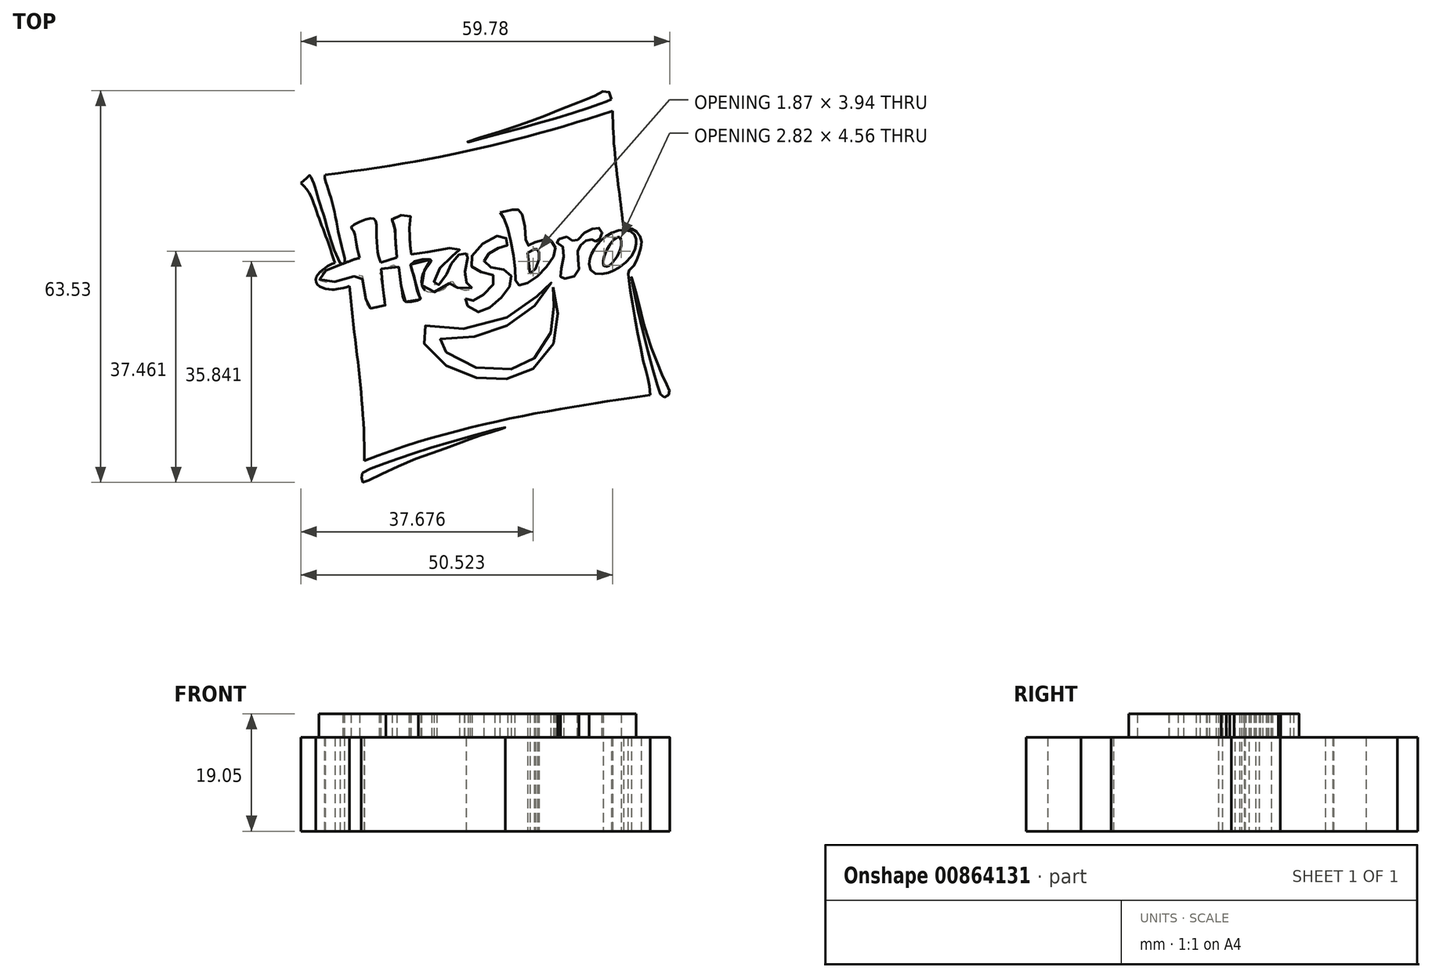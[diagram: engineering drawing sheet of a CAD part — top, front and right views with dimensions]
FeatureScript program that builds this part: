
annotation { "Feature Type Name" : "Feature", "Feature Type Description" : "" }
export const myFeature = defineFeature(function(context is Context, id is Id, definition is map)
    precondition{}
    {
        {
            var Q0;
            Q0=qCreatedBy(makeId("Top.planeOp"),FACE);
            var sketch = newSketch(context, id + "F0", { "sketchPlane" : qUnion([Q0])});
            skFitSpline(sketch, "E0", {"points": [v(-6.58, -8.68) * mm, v(-52.97, -19.35) * mm], "startDerivative": vector(-37.99, -5.76) * mm, "endDerivative": vector(-49.48, -19.31) * mm});
            skFitSpline(sketch, "E1", {"points": [v(-52.97, -19.35) * mm, v(-55.37, 8.98) * mm], "startDerivative": vector(0.45, 28.63) * mm, "endDerivative": vector(-2.64, 28.98) * mm});
            skFitSpline(sketch, "E2", {"points": [v(-55.37, 8.98) * mm, v(-57.18, 8.5) * mm, v(-58.16, 8.4) * mm, v(-60.34, 8.98) * mm, v(-60.78, 10.31) * mm, v(-59.22, 11.97) * mm, v(-57.72, 12.68) * mm], "startDerivative": vector(-11.74, -5.94) * mm, "endDerivative": vector(11.13, 2.82) * mm});
            skFitSpline(sketch, "E3", {"points": [v(-57.72, 12.68) * mm, v(-59.05, 16.69) * mm, v(-60.65, 20.96) * mm, v(-63.22, 25.68) * mm], "startDerivative": vector(-4.13, 12.53) * mm, "endDerivative": vector(-12.66, 11.1) * mm});
            skFitSpline(sketch, "E4", {"points": [v(-63.22, 25.68) * mm, v(-61.72, 26.83) * mm, v(-61.17, 25.68) * mm, v(-60.46, 23.36) * mm, v(-59.3, 19.62) * mm, v(-58.15, 15.7) * mm, v(-56.9, 12.68) * mm], "startDerivative": vector(28.8, 24.8) * mm, "endDerivative": vector(6.95, -15.78) * mm});
            skFitSpline(sketch, "E5", {"points": [v(-56.9, 12.68) * mm, v(-56.2, 12.68) * mm, v(-56.82, 16.24) * mm, v(-58.16, 22.47) * mm, v(-59.3, 26.3) * mm, v(-59.3, 27.01) * mm], "startDerivative": vector(7.9, -2.42) * mm, "endDerivative": vector(0.66, 6.97) * mm});
            skFitSpline(sketch, "E6", {"points": [v(-59.3, 27.01) * mm, v(-12.67, 37.35) * mm], "startDerivative": vector(48.86, 5.62) * mm, "endDerivative": vector(45.12, 14.97) * mm});
            skFitSpline(sketch, "E7", {"points": [v(-12.67, 37.35) * mm, v(-10.9, 18.3) * mm], "startDerivative": vector(-0.01, -20.56) * mm, "endDerivative": vector(1.86, -17.62) * mm});
            skFitSpline(sketch, "E8", {"points": [v(-10.9, 18.3) * mm, v(-9.74, 18.3) * mm, v(-8.14, 16.88) * mm, v(-8.4, 14.2) * mm, v(-9.48, 11.98) * mm, v(-10.01, 11.54) * mm, v(-10.01, 9.67) * mm, v(-7.62, -3.5) * mm, v(-6.58, -8.68) * mm], "startDerivative": vector(14, 2.58) * mm, "endDerivative": vector(2.8, -38.94) * mm});
            skFitSpline(sketch, "E9", {"points": [v(-12.9, 39.26) * mm, v(-13.46, 40.6) * mm, v(-14.95, 40.12) * mm, v(-17.69, 38.95) * mm, v(-23.43, 36.65) * mm, v(-30, 34.3) * mm, v(-36.44, 32.26) * mm, v(-31.25, 33.58) * mm, v(-22, 36.14) * mm, v(-15.12, 38.35) * mm, v(-13.61, 38.91) * mm, v(-12.9, 39.26) * mm]});
            skFitSpline(sketch, "E10", {"points": [v(-53.26, -21.34) * mm, v(-48.92, -19.5) * mm, v(-40.24, -16.67) * mm, v(-30.06, -13.94) * mm, v(-31.06, -14.32) * mm, v(-34.59, -15.39) * mm, v(-38.82, -17) * mm, v(-46.28, -19.74) * mm, v(-52.85, -22.8) * mm, v(-53.24, -22.77) * mm, v(-53.41, -21.9) * mm, v(-53.26, -21.34) * mm]});
            skFitSpline(sketch, "E11", {"points": [v(-4.32, -9.04) * mm, v(-5.54, -6.78) * mm, v(-9.35, 8.63) * mm, v(-9.6, 10.43) * mm, v(-9.35, 9.53) * mm, v(-8.4, 5.94) * mm, v(-6.97, 0.62) * mm, v(-3.9, -7.06) * mm, v(-3.48, -8.45) * mm, v(-4.32, -9.04) * mm]});
            skFitSpline(sketch, "E12", {"points": [v(-22.31, 8.79) * mm, v(-22.43, 8.75) * mm, v(-22.63, 8.68) * mm, v(-22.41, 7.43) * mm, v(-22.26, 4.06) * mm, v(-22.52, 2.25) * mm, v(-23.3, -0.3) * mm, v(-25.36, -2.72) * mm, v(-27.15, -3.77) * mm, v(-29.33, -4.56) * mm, v(-33.46, -4.59) * mm, v(-37.14, -3.4) * mm, v(-39.95, -1.48) * mm, v(-41.04, 0.08) * mm, v(-41.15, 0.35) * mm, v(-40.38, 0.35) * mm, v(-36.74, 0.49) * mm, v(-32.3, 1.49) * mm, v(-29.3, 2.88) * mm, v(-26.01, 5.17) * mm, v(-23.83, 7.46) * mm, v(-22.63, 9.46) * mm, v(-22.71, 9.59) * mm, v(-22.9, 9.54) * mm, v(-23.97, 8.31) * mm, v(-26.48, 5.97) * mm, v(-30.83, 3.42) * mm, v(-37.34, 1.96) * mm, v(-42.27, 2.26) * mm, v(-44.06, 2.68) * mm, v(-43.53, 0.22) * mm, v(-41.72, -2.4) * mm, v(-39.1, -4.26) * mm, v(-35.87, -5.65) * mm, v(-32.64, -6.18) * mm, v(-29.81, -6.08) * mm, v(-27.33, -5.4) * mm, v(-24.87, -3.91) * mm, v(-22.55, -1) * mm, v(-21.8, 1.35) * mm, v(-21.57, 4.76) * mm, v(-22.01, 8) * mm, v(-22.31, 8.79) * mm]});
            skLineSegment(sketch, "E13", {"start": v(-26.1, 11.01) * mm, "end": v(-26.48, 14.37) * mm});
            skLineSegment(sketch, "E14", {"start": v(-26.48, 14.37) * mm, "end": v(-25.38, 14.93) * mm});
            skLineSegment(sketch, "E15", {"start": v(-25.38, 14.93) * mm, "end": v(-24.9, 14.95) * mm});
            skLineSegment(sketch, "E16", {"start": v(-24.9, 14.95) * mm, "end": v(-24.61, 14.37) * mm});
            skLineSegment(sketch, "E17", {"start": v(-24.61, 14.37) * mm, "end": v(-24.61, 13.3) * mm});
            skLineSegment(sketch, "E18", {"start": v(-24.61, 13.3) * mm, "end": v(-25.2, 11.76) * mm});
            skLineSegment(sketch, "E19", {"start": v(-25.2, 11.76) * mm, "end": v(-26.1, 11.01) * mm});
            skFitSpline(sketch, "E20", {"points": [v(-30.9, 20.91) * mm, v(-30.15, 21.09) * mm, v(-29.03, 21.33) * mm, v(-28.18, 21.39) * mm, v(-27.56, 21.01) * mm, v(-26.83, 17.65) * mm, v(-26.45, 15.57) * mm, v(-25.38, 16.02) * mm, v(-23.4, 16.47) * mm, v(-22.16, 15.78) * mm, v(-22.1, 14.14) * mm, v(-24.3, 11.08) * mm, v(-27.04, 9.24) * mm, v(-28.25, 9.3) * mm, v(-28.5, 11.67) * mm, v(-29.27, 16.53) * mm, v(-30.36, 20.06) * mm, v(-30.9, 20.91) * mm]});
            skFitSpline(sketch, "E21", {"points": [v(-15.4, 16.2) * mm, v(-15.81, 16.4) * mm, v(-16.63, 16.49) * mm, v(-17.65, 15.78) * mm, v(-18.32, 14.78) * mm, v(-18.24, 12.94) * mm, v(-18.49, 10.82) * mm, v(-20.61, 10.19) * mm, v(-21.13, 10.47) * mm, v(-20.8, 12.63) * mm, v(-20.87, 15.5) * mm, v(-21.83, 16.11) * mm, v(-21.17, 16.66) * mm, v(-19.76, 16.83) * mm, v(-18.9, 16.17) * mm, v(-17.5, 17.35) * mm, v(-15.75, 18.3) * mm, v(-14.68, 18.27) * mm, v(-14.4, 17.37) * mm, v(-14.94, 16.4) * mm, v(-15.4, 16.2) * mm]});
            skFitSpline(sketch, "E22", {"points": [v(-36.54, 6.92) * mm, v(-35.6, 6.6) * mm, v(-34.02, 7.23) * mm, v(-31.88, 9.5) * mm, v(-32.1, 10.76) * mm, v(-34.6, 11.38) * mm, v(-35.69, 12.55) * mm, v(-34.96, 14.7) * mm, v(-31.27, 17.12) * mm, v(-30, 16.78) * mm, v(-29.67, 15.61) * mm, v(-30.34, 15.5) * mm, v(-32.08, 14.62) * mm, v(-33.25, 13.8) * mm, v(-33.41, 12.54) * mm, v(-31.46, 11.84) * mm, v(-29.46, 11.14) * mm, v(-29.13, 9.72) * mm, v(-30.25, 7.6) * mm, v(-33.03, 5.24) * mm, v(-34.95, 4.86) * mm, v(-36.6, 6.44) * mm, v(-36.54, 6.92) * mm]});
            skFitSpline(sketch, "E23", {"points": [v(-35.46, 8.67) * mm, v(-36.08, 9.14) * mm, v(-36.62, 10.19) * mm, v(-36.36, 12.83) * mm, v(-36.16, 14.22) * mm, v(-36.42, 14.2) * mm, v(-36.75, 14.4) * mm, v(-38.1, 13.63) * mm, v(-39.01, 12.21) * mm, v(-39.96, 10.26) * mm, v(-41.28, 8.97) * mm, v(-41.67, 9.63) * mm, v(-40.14, 12.55) * mm, v(-37.77, 14.5) * mm, v(-37.5, 14.93) * mm, v(-40.11, 14.96) * mm, v(-45.32, 14.12) * mm, v(-45.48, 14.72) * mm, v(-45.66, 18.29) * mm, v(-45.44, 20.27) * mm, v(-46.66, 20.5) * mm, v(-48.39, 19.95) * mm, v(-48.1, 18.82) * mm, v(-47.9, 16.75) * mm, v(-47.66, 13.6) * mm], "startDerivative": vector(-21.22, 14.36) * mm, "endDerivative": vector(5.81, -56.54) * mm});
            skLineSegment(sketch, "E24", {"start": v(-47.66, 13.6) * mm, "end": v(-50.3, 12.8) * mm});
            skFitSpline(sketch, "E25", {"points": [v(-50.3, 12.8) * mm, v(-50.7, 14.04) * mm, v(-50.95, 16.92) * mm, v(-51.19, 19.65) * mm, v(-52.2, 19.89) * mm, v(-55.08, 18.53) * mm, v(-54.72, 17.96) * mm, v(-54.24, 15.88) * mm, v(-53.72, 13.51) * mm], "startDerivative": vector(-4.3, 10.85) * mm, "endDerivative": vector(4.27, -16.4) * mm});
            skFitSpline(sketch, "E26", {"points": [v(-53.72, 13.51) * mm, v(-54.72, 13.23) * mm, v(-56.2, 12.68) * mm, v(-58.41, 11.9) * mm, v(-59.81, 11.09) * mm, v(-60.28, 10.34) * mm, v(-59.75, 9.65) * mm, v(-57.72, 9.68) * mm, v(-55.08, 10.37) * mm, v(-53.37, 10.84) * mm, v(-53.27, 10.43) * mm, v(-52.8, 7.5) * mm, v(-52.56, 6.04) * mm, v(-52.3, 5.45) * mm, v(-51.19, 5.42) * mm, v(-49.6, 5.8) * mm, v(-49.47, 6.32) * mm, v(-50.3, 10.37) * mm, v(-50.3, 11.65) * mm, v(-47.66, 12.33) * mm, v(-47.3, 11.15) * mm, v(-46.83, 8.13) * mm, v(-46.4, 6.5) * mm, v(-45.55, 6.42) * mm, v(-43.84, 6.88) * mm, v(-44.15, 7.54) * mm, v(-45, 10.9) * mm, v(-45.27, 12.68) * mm, v(-42.1, 13.23) * mm, v(-42.22, 12.8) * mm, v(-43.37, 11.15) * mm, v(-43.65, 9.8) * mm, v(-43.34, 8.47) * mm, v(-41.57, 7.97) * mm, v(-39.67, 8.81) * mm, v(-38.73, 9.75) * mm, v(-38.33, 9.16) * mm, v(-36.46, 8.31) * mm, v(-35.46, 8.67) * mm, v(-35.66, 8.8) * mm], "startDerivative": vector(-45.95, -11.43) * mm, "endDerivative": vector(-29.98, 11.17) * mm});
            skFitSpline(sketch, "E27", {"points": [v(-12.64, 11.44) * mm, v(-13.78, 11.04) * mm, v(-15.73, 11.07) * mm, v(-16.47, 12.41) * mm, v(-16.3, 13.69) * mm, v(-15.81, 14.76) * mm, v(-14.92, 15.94) * mm, v(-13.81, 17.01) * mm, v(-11.83, 17.92) * mm, v(-10.09, 17.95) * mm, v(-9.08, 17.25) * mm, v(-8.88, 16.4) * mm, v(-9.01, 15.07) * mm, v(-10.46, 12.85) * mm, v(-12.64, 11.44) * mm]});
            skFitSpline(sketch, "E28", {"points": [v(-11.51, 16.88) * mm, v(-12.18, 16.72) * mm, v(-12.8, 16.1) * mm, v(-13.72, 14.63) * mm, v(-14.16, 12.44) * mm, v(-13.6, 12.12) * mm, v(-12.06, 13.59) * mm, v(-11.27, 15.8) * mm, v(-11.51, 16.88) * mm]});
            skSolve(sketch);
        }
        {
            var Q0;
            {var subQ0=sQuery(id+"F0.wireOp",EDGE,"E24");Q0=makeQuery(id+"F0.imprint","IMPRINT",FACE,{"disambiguationData":[TD([[makeQuery(id+"F0.imprint","IMPRINT",EDGE,{"derivedFrom":subQ0}),1.0]])]});}
            var Q1;
            Q1=makeQuery(id+"F0.imprint","IMPRINT",FACE,{"disambiguationData":[TD([[makeQuery(id+"F0.imprint","IMPRINT",EDGE,{"derivedFrom":sQuery(id+"F0.wireOp",EDGE,"E22")}),-1.0]])]});
            var Q2;
            Q2=makeQuery(id+"F0.imprint","IMPRINT",FACE,{"disambiguationData":[TD([[makeQuery(id+"F0.imprint","IMPRINT",EDGE,{"derivedFrom":sQuery(id+"F0.wireOp",EDGE,"E13")}),1.0]])]});
            var Q3;
            Q3=makeQuery(id+"F0.imprint","IMPRINT",FACE,{"disambiguationData":[TD([[makeQuery(id+"F0.imprint","IMPRINT",EDGE,{"derivedFrom":sQuery(id+"F0.wireOp",EDGE,"E21")}),-1.0]])]});
            var Q4;
            Q4=makeQuery(id+"F0.imprint","IMPRINT",FACE,{"disambiguationData":[TD([[makeQuery(id+"F0.imprint","IMPRINT",EDGE,{"derivedFrom":sQuery(id+"F0.wireOp",EDGE,"E27")}),-1.0]])]});
            var Q5;
            Q5=makeQuery(id+"F0.imprint","IMPRINT",FACE,{"disambiguationData":[TD([[makeQuery(id+"F0.imprint","IMPRINT",EDGE,{"derivedFrom":sQuery(id+"F0.wireOp",EDGE,"E12")}),1.0]])]});
            extrude(context, id + "F1", {"entities" : qUnion([Q0, Q1, Q2, Q3, Q4, Q5]), "depth" : 19.05 * mm, "offsetDistance" : 25.4 * mm});
        }
        {
            var Q0;
            Q0=makeQuery(id+"F0.imprint","IMPRINT",FACE,{"disambiguationData":[TD([[makeQuery(id+"F0.imprint","IMPRINT",EDGE,{"derivedFrom":sQuery(id+"F0.wireOp",EDGE,"E9")}),1.0]])]});
            var Q1;
            Q1=makeQuery(id+"F0.imprint","IMPRINT",FACE,{"disambiguationData":[TD([[makeQuery(id+"F0.imprint","IMPRINT",EDGE,{"derivedFrom":sQuery(id+"F0.wireOp",EDGE,"E11")}),-1.0]])]});
            var Q2;
            Q2=makeQuery(id+"F0.imprint","IMPRINT",FACE,{"disambiguationData":[TD([[makeQuery(id+"F0.imprint","IMPRINT",EDGE,{"derivedFrom":sQuery(id+"F0.wireOp",EDGE,"E10")}),-1.0]])]});
            var Q3;
            Q3=makeQuery(id+"F0.imprint","IMPRINT",FACE,{"disambiguationData":[TD([[makeQuery(id+"F0.imprint","IMPRINT",EDGE,{"derivedFrom":sQuery(id+"F0.wireOp",EDGE,"E0")}),-1.0]])]});
            extrude(context, id + "F2", {"entities" : qUnion([Q0, Q1, Q2, Q3]), "operationType" : NewBodyOperationType.ADD, "depth" : 15.24 * mm, "offsetDistance" : 25.4 * mm});
        }
    });
